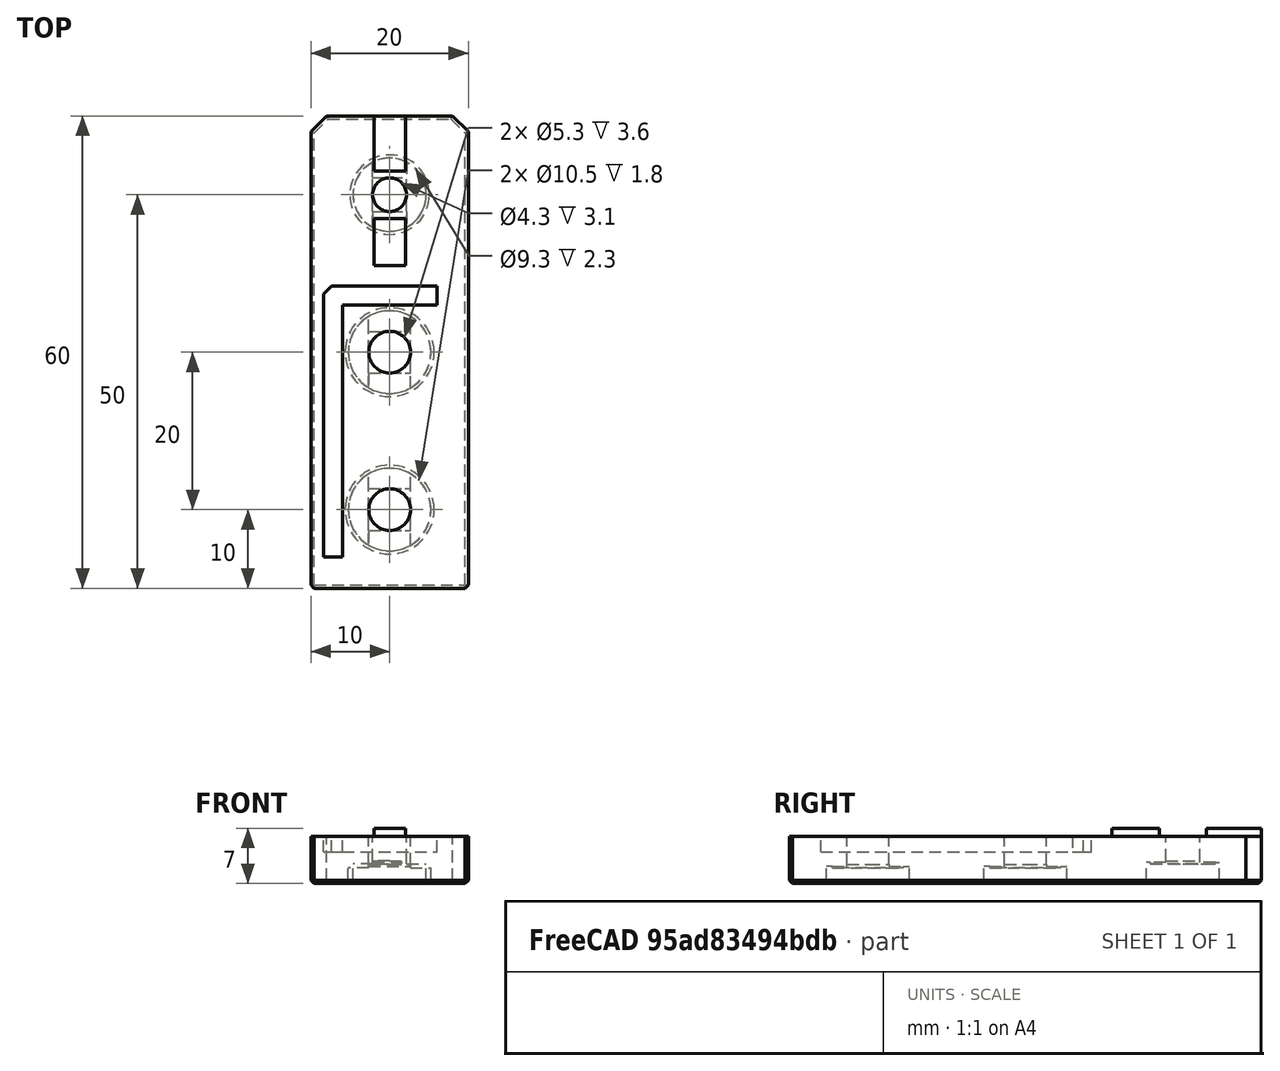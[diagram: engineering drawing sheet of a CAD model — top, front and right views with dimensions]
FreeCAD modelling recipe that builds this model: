
FCSTD DOCUMENT  (FreeCAD 0.18R14555 (Git shallow))
Label: z-cap-connector
License: All rights reserved
LicenseURL: http://en.wikipedia.org/wiki/All_rights_reserved
objects: Part::Box×9, Part::MultiFuse×7, Part::Cut×7, Part::Cylinder×6, Part::Chamfer×3, Part::Feature×2
note: 34 computed .brp shape members not serialized (recipe doc carries the construction recipe); baked Part::Feature solids carry a one-line shape summary decoded from their .brp

FEATURE [Part::Box] Box  label="Cube"
  AttacherType = Attacher::AttachEngine3D
  Height = 6
  Length = 20
  Width = 60
FEATURE [Part::Cylinder] Cylinder
  Angle = 360
  AttacherType = Attacher::AttachEngine3D
  Height = 2.4
  Placement = pos=(10,10,0) rot=(0,0,1;0rad)
  Radius = 5.25
FEATURE [Part::Cylinder] Cylinder001
  Angle = 360
  AttacherType = Attacher::AttachEngine3D
  Height = 2.4
  Placement = pos=(10,30,0) rot=(0,0,1;0rad)
  Radius = 5.25
FEATURE [Part::Cylinder] Cylinder002
  Angle = 360
  AttacherType = Attacher::AttachEngine3D
  Height = 2.9
  Placement = pos=(10,50,0) rot=(0,0,1;0rad)
  Radius = 4.65
FEATURE [Part::Cylinder] Cylinder005
  Angle = 360
  AttacherType = Attacher::AttachEngine3D
  Height = 10
  Placement = pos=(10,10,0) rot=(0,0,1;0rad)
  Radius = 2.65
FEATURE [Part::Cylinder] Cylinder007
  Angle = 360
  AttacherType = Attacher::AttachEngine3D
  Height = 10
  Placement = pos=(10,30,0) rot=(0,0,1;0rad)
  Radius = 2.65
FEATURE [Part::Cylinder] Cylinder008
  Angle = 360
  AttacherType = Attacher::AttachEngine3D
  Height = 10
  Placement = pos=(10,50,0) rot=(0,0,1;0rad)
  Radius = 2.15
FEATURE [Part::Box] Box009  label="Cube009"
  AttacherType = Attacher::AttachEngine3D
  Height = 0.2
  Length = 10
  Placement = pos=(-5,2.15,0.2) rot=(0,0,1;0rad)
  Width = 5
FEATURE [Part::Box] Box010  label="Cube010"
  AttacherType = Attacher::AttachEngine3D
  Height = 0.4
  Length = 5
  Placement = pos=(-7.15,-5,0) rot=(0,0,1;0rad)
  Width = 10
FEATURE [Part::Box] Box011  label="Cube011"
  AttacherType = Attacher::AttachEngine3D
  Height = 0.2
  Length = 10
  Placement = pos=(-5,-7.15,0.2) rot=(0,0,1;0rad)
  Width = 5
FEATURE [Part::Box] Box012  label="Cube012"
  AttacherType = Attacher::AttachEngine3D
  Height = 0.4
  Length = 5
  Placement = pos=(2.15,-5,0) rot=(0,0,1;0rad)
  Width = 10
FEATURE [Part::Feature] Fusion001001  label="Fusion002"
  Placement = pos=(10,30,2) rot=(0,0,1;0rad)
  shape: bbox 15.3 x 15.3 x 0.4 mm, 28 faces (baked)
FEATURE [Part::Feature] Fusion001002  label="Fusion003"
  Placement = pos=(10,10,2) rot=(0,0,1;0rad)
  shape: bbox 15.3 x 15.3 x 0.4 mm, 28 faces (baked)
FEATURE [Part::MultiFuse] Fusion001005
  Placement = pos=(10,50,2.5) rot=(0,0,1;0rad)
  Shapes = -> [Box012,Box009,Box010,Box011]
FEATURE [Part::Box] Box013  label="Cube013"
  AttacherType = Attacher::AttachEngine3D
  Height = 2
  Length = 2.4
  Placement = pos=(1.6,4,4) rot=(0,0,1;0rad)
  Width = 34.4
FEATURE [Part::Box] Box014  label="Cube014"
  AttacherType = Attacher::AttachEngine3D
  Height = 2
  Length = 14.4
  Placement = pos=(1.6,36,4) rot=(0,0,1;0rad)
  Width = 2.4
FEATURE [Part::MultiFuse] Fusion001007
  Shapes = -> [Box014,Box013]
FEATURE [Part::Chamfer] Chamfer
  Base = -> Fusion001007
  Edges = 1 edges r=1: [Edge3]
FEATURE [Part::Box] Box015  label="Cube015"
  AttacherType = Attacher::AttachEngine3D
  Height = 1
  Length = 4
  Placement = pos=(8,41,6) rot=(0,0,1;0rad)
  Width = 6
FEATURE [Part::Box] Box016  label="Cube016"
  AttacherType = Attacher::AttachEngine3D
  Height = 1
  Length = 4
  Placement = pos=(8,53,6) rot=(0,0,1;0rad)
  Width = 7
FEATURE [Part::Cut] Cut
  Base = -> Box
  Tool = -> Cylinder005
FEATURE [Part::Cut] Cut001
  Base = -> Cut
  Tool = -> Cylinder007
FEATURE [Part::Cut] Cut002
  Base = -> Cut001
  Tool = -> Cylinder
FEATURE [Part::Cut] Cut003
  Base = -> Cut002
  Tool = -> Cylinder001
FEATURE [Part::Cut] Cut004
  Base = -> Cut003
  Tool = -> Cylinder008
FEATURE [Part::Cut] Cut005
  Base = -> Cut004
  Tool = -> Cylinder002
FEATURE [Part::MultiFuse] Fusion
  Shapes = -> [Cut005,Fusion001002]
FEATURE [Part::MultiFuse] Fusion001008
  Shapes = -> [Fusion,Fusion001001]
FEATURE [Part::MultiFuse] Fusion001009
  Shapes = -> [Fusion001008,Fusion001005]
FEATURE [Part::MultiFuse] Fusion001010
  Shapes = -> [Fusion001009,Box015]
FEATURE [Part::MultiFuse] Fusion001011
  Shapes = -> [Fusion001010,Box016]
FEATURE [Part::Cut] Cut006
  Base = -> Fusion001011
  Tool = -> Chamfer
FEATURE [Part::Chamfer] Chamfer001
  Base = -> Cut006
  Edges = 2 edges r=2: [Edge3,Edge31]
FEATURE [Part::Chamfer] Chamfer002
  Base = -> Chamfer001
  Edges = 11 edges r=0.4: [Edge3,Edge4,Edge30,Edge32,Edge33,Edge34,Edge35,Edge36,Edge37,Edge38,Edge39]
